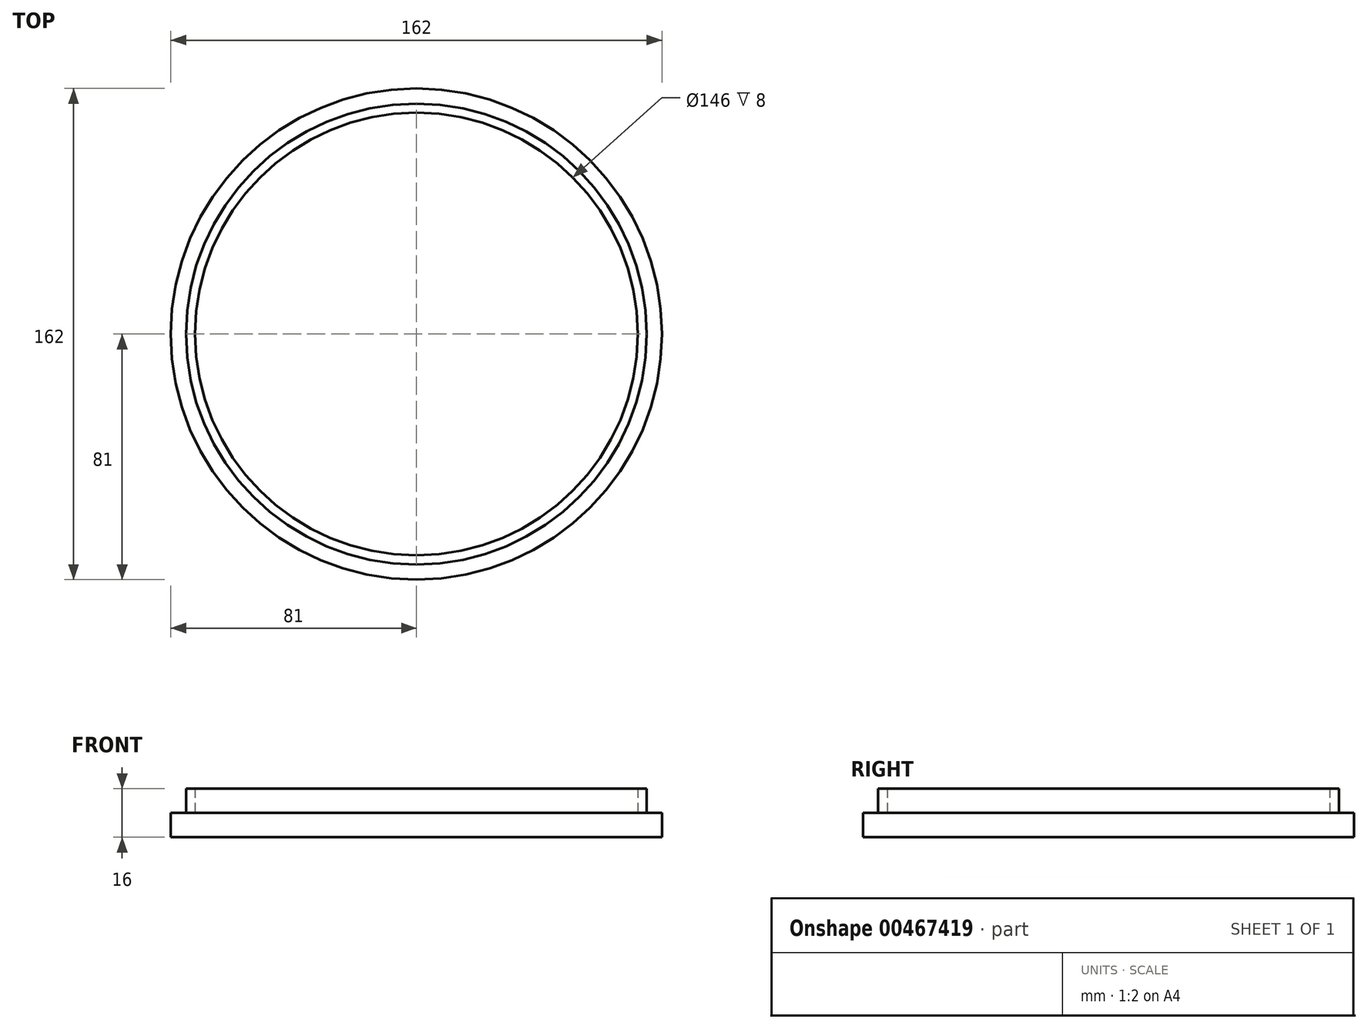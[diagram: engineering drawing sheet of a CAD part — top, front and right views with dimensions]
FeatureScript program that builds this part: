
annotation { "Feature Type Name" : "Feature", "Feature Type Description" : "" }
export const myFeature = defineFeature(function(context is Context, id is Id, definition is map)
    precondition{}
    {
        {
            var Q0;
            Q0=qCreatedBy(makeId("Top.planeOp"),FACE);
            var sketch = newSketch(context, id + "F0", { "sketchPlane" : qUnion([Q0])});
            skCircle(sketch, "E0", {"center": v(0, 0) * mm, "radius": 79 * mm});
            skCircle(sketch, "E1", {"center": v(0, 0) * mm, "radius": 81 * mm});
            skCircle(sketch, "E2", {"center": v(0, 0) * mm, "radius": 76 * mm});
            skCircle(sketch, "E3", {"center": v(0, 0) * mm, "radius": 27.9 * mm});
            skCircle(sketch, "E4", {"center": v(0, 0) * mm, "radius": 73 * mm});
            skSolve(sketch);
        }
        {
            var Q0;
            Q0=makeQuery(id+"F0.imprint","IMPRINT",FACE,{"disambiguationData":[TD([[makeQuery(id+"F0.imprint","IMPRINT",EDGE,{"derivedFrom":sQuery(id+"F0.wireOp",EDGE,"E2")}),1.0]])]});
            extrude(context, id + "F1", {"entities" : qUnion([Q0]), "depth" : 8 * mm, "offsetDistance" : 25 * mm});
        }
        {
            var Q0;
            Q0=makeQuery(id+"F0.imprint","IMPRINT",FACE,{"disambiguationData":[TD([[makeQuery(id+"F0.imprint","IMPRINT",EDGE,{"derivedFrom":sQuery(id+"F0.wireOp",EDGE,"E0")}),-1.0]])]});
            var Q1;
            Q1=makeQuery(id+"F0.imprint","IMPRINT",FACE,{"disambiguationData":[TD([[makeQuery(id+"F0.imprint","IMPRINT",EDGE,{"derivedFrom":sQuery(id+"F0.wireOp",EDGE,"E0")}),1.0]])]});
            var Q2;
            Q2=makeQuery(id+"F0.imprint","IMPRINT",FACE,{"disambiguationData":[TD([[makeQuery(id+"F0.imprint","IMPRINT",EDGE,{"derivedFrom":sQuery(id+"F0.wireOp",EDGE,"E2")}),1.0]])]});
            var Q3;
            Q3=makeQuery(id+"F0.imprint","IMPRINT",FACE,{"disambiguationData":[TD([[makeQuery(id+"F0.imprint","IMPRINT",EDGE,{"derivedFrom":sQuery(id+"F0.wireOp",EDGE,"E3")}),-1.0]])]});
            var Q4;
            Q4=makeQuery(id+"F0.imprint","IMPRINT",FACE,{"disambiguationData":[TD([[makeQuery(id+"F0.imprint","IMPRINT",EDGE,{"derivedFrom":sQuery(id+"F0.wireOp",EDGE,"E3")}),1.0]])]});
            extrude(context, id + "F2", {"entities" : qUnion([Q0, Q1, Q2, Q3, Q4]), "operationType" : NewBodyOperationType.ADD, "oppositeDirection" : true, "depth" : 8 * mm, "offsetDistance" : 25 * mm});
        }
    });
